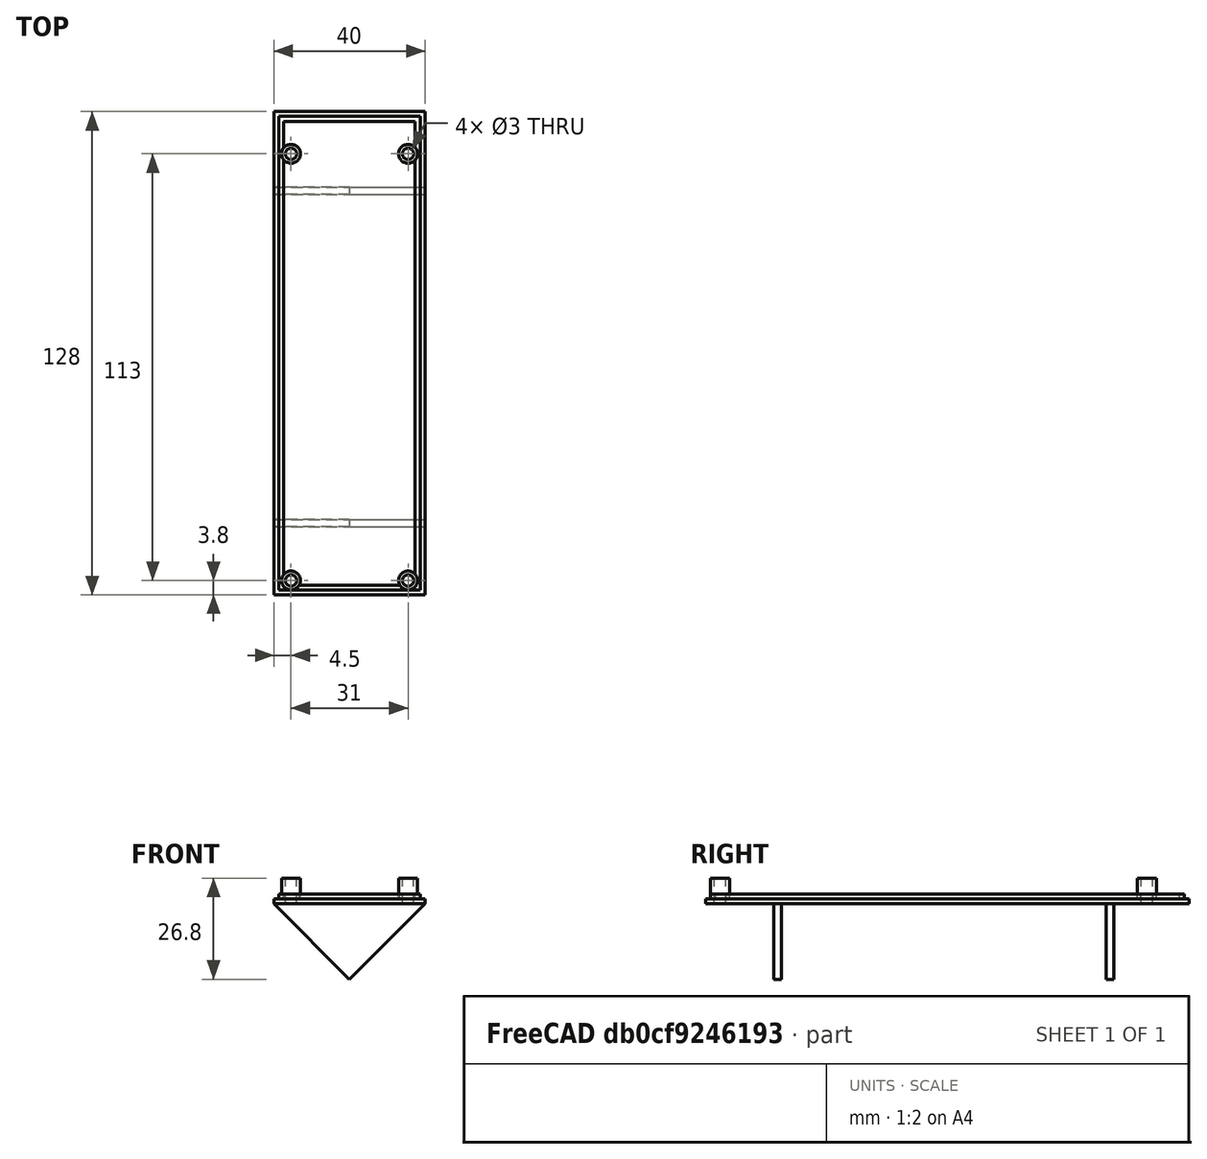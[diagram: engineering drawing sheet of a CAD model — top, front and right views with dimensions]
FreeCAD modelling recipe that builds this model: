
FCSTD DOCUMENT  (FreeCAD 0.18R4 (GitTag))
Label: LCD back-v2
License: All rights reserved
LicenseURL: http://en.wikipedia.org/wiki/All_rights_reserved
objects: Part::FeaturePython×6, Part::MultiFuse×4, Part::Box×3, Part::Cut×2, Part::Cylinder×2, Part::Wedge×2
note: 19 computed .brp shape members not serialized (recipe doc carries the construction recipe); baked Part::Feature solids carry a one-line shape summary decoded from their .brp

FEATURE [Part::Box] Box  label="Back plate"
  AttacherType = Attacher::AttachEngine3D
  Height = 1.3
  Length = 40
  Width = 128
FEATURE [Part::Box] Box001  label="Wall outer"
  AttacherType = Attacher::AttachEngine3D
  Height = 1.3
  Length = 37.4
  Placement = pos=(1.3,1.3,1.3) rot=(0,0,1;0rad)
  Width = 125.4
FEATURE [Part::Box] Box002  label="Wall cutout"
  AttacherType = Attacher::AttachEngine3D
  Height = 1.3
  Length = 34.8
  Placement = pos=(2.6,2.6,1.3) rot=(0,0,1;0rad)
  Width = 122.8
FEATURE [Part::Cut] Cut  label="Wall"
  Base = -> Box001
  Tool = -> Box002
FEATURE [Part::Cylinder] Cylinder  label="Board post 1"
  Angle = 360
  AttacherType = Attacher::AttachEngine3D
  Height = 6.8
  Placement = pos=(4.5,3.8,0) rot=(0,0,1;0rad)
  Radius = 2.5
FEATURE [Part::FeaturePython] Clone001  label="Board post 3"  # Draft clone (typed FeaturePython)
  AttacherType = Attacher::AttachEngine3D
  Fuse = false
  Objects = -> [Cylinder]
  Placement = pos=(4.5,116.8,0) rot=(0,0,1;0rad)
  Scale = (1,1,1)
FEATURE [Part::FeaturePython] Clone  label="Board post 2"  # Draft clone (typed FeaturePython)
  AttacherType = Attacher::AttachEngine3D
  Fuse = false
  Objects = -> [Cylinder]
  Placement = pos=(35.5,3.8,0) rot=(0,0,1;0rad)
  Scale = (1,1,1)
FEATURE [Part::FeaturePython] Clone002  label="Board post 4"  # Draft clone (typed FeaturePython)
  AttacherType = Attacher::AttachEngine3D
  Fuse = false
  Objects = -> [Cylinder]
  Placement = pos=(35.5,116.8,0) rot=(0,0,1;0rad)
  Scale = (1,1,1)
FEATURE [Part::MultiFuse] Fusion  label="Board posts"
  Shapes = -> [Cylinder,Clone001,Clone,Clone002]
FEATURE [Part::Cylinder] Cylinder001  label="Board post drill 1"
  Angle = 360
  AttacherType = Attacher::AttachEngine3D
  Height = 6.8
  Placement = pos=(4.5,3.8,0) rot=(0,0,1;0rad)
  Radius = 1.5
FEATURE [Part::FeaturePython] Clone003  label="Board post drill 2"  # Draft clone (typed FeaturePython)
  AttacherType = Attacher::AttachEngine3D
  Fuse = false
  Objects = -> [Cylinder001]
  Placement = pos=(35.5,3.8,0) rot=(0,0,1;0rad)
  Scale = (1,1,1)
FEATURE [Part::FeaturePython] Clone004  label="Board post drill 3"  # Draft clone (typed FeaturePython)
  AttacherType = Attacher::AttachEngine3D
  Fuse = false
  Objects = -> [Cylinder001]
  Placement = pos=(4.5,116.8,0) rot=(0,0,1;0rad)
  Scale = (1,1,1)
FEATURE [Part::FeaturePython] Clone005  label="Board post drill 4"  # Draft clone (typed FeaturePython)
  AttacherType = Attacher::AttachEngine3D
  Fuse = false
  Objects = -> [Cylinder001]
  Placement = pos=(35.5,116.8,0) rot=(0,0,1;0rad)
  Scale = (1,1,1)
FEATURE [Part::MultiFuse] Fusion001  label="Board post drills"
  Shapes = -> [Clone005,Cylinder001,Clone003,Clone004]
FEATURE [Part::MultiFuse] Fusion002  label="Plate plus wall and posts"
  Shapes = -> [Box,Fusion,Cut]
FEATURE [Part::Cut] Cut001  label="Back plate plus wall and posts drilled."
  Base = -> Fusion002
  Tool = -> Fusion001
FEATURE [Part::Wedge] Wedge  label="Support 1"
  AttacherType = Attacher::AttachEngine3D
  Placement = pos=(20,20,-20) rot=(0.357407,-0.357407,-0.862856;1.71775rad)
  X2max = 2
  X2min = 0
  Xmax = 2
  Xmin = 0
  Ymax = 28.28
  Ymin = 0
  Z2max = 0
  Z2min = 0
  Zmax = 28.28
  Zmin = 0
FEATURE [Part::Wedge] Wedge001  label="Support 2"
  AttacherType = Attacher::AttachEngine3D
  Placement = pos=(20,108,-20) rot=(0.357407,-0.357407,-0.862856;1.71775rad)
  X2max = 2
  X2min = 0
  Xmax = 2
  Xmin = 0
  Ymax = 28.28
  Ymin = 0
  Z2max = 0
  Z2min = 0
  Zmax = 28.28
  Zmin = 0
FEATURE [Part::MultiFuse] Fusion003  label="Back plate plus supports"
  Shapes = -> [Cut001,Wedge001,Wedge]
